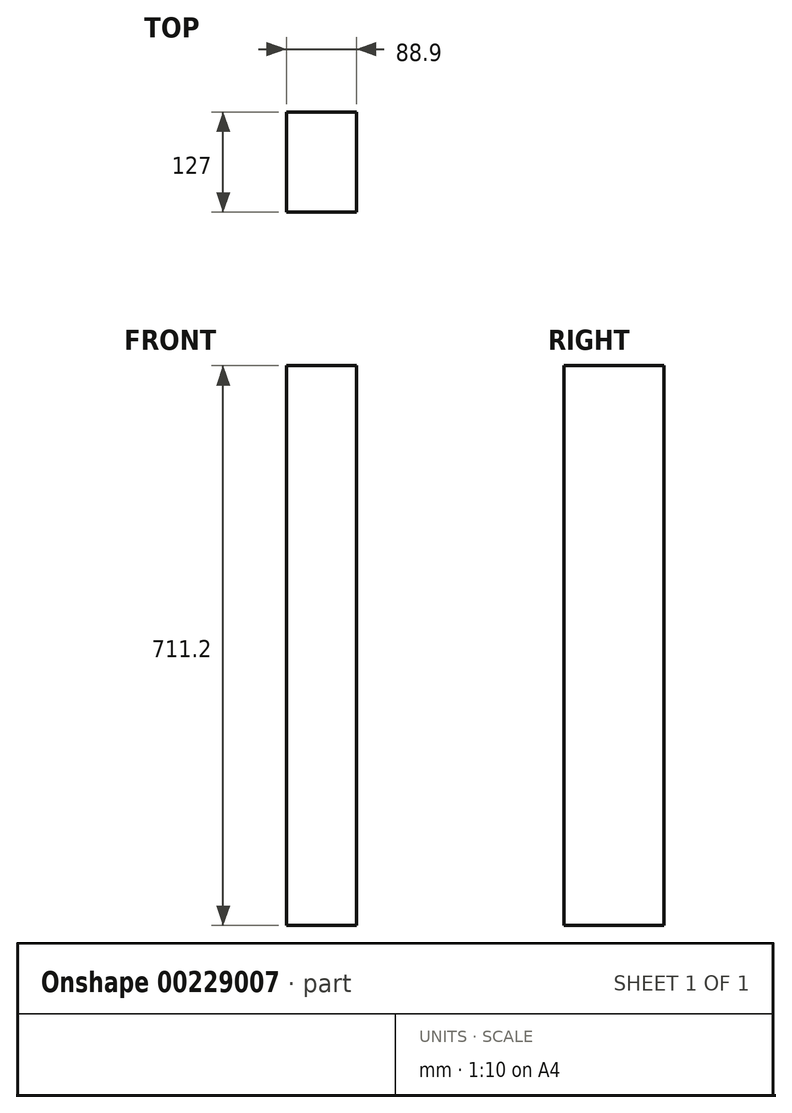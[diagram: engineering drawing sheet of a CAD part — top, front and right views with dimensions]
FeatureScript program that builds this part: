
annotation { "Feature Type Name" : "Feature", "Feature Type Description" : "" }
export const myFeature = defineFeature(function(context is Context, id is Id, definition is map)
    precondition{}
    {
        {
            var Q0;
            Q0=qCreatedBy(makeId("Top.planeOp"),FACE);
            var sketch = newSketch(context, id + "F0", { "sketchPlane" : qUnion([Q0])});
            skLineSegment(sketch, "E0.bottom", {"start": v(-42.17, 67) * mm, "end": v(46.73, 67) * mm});
            skLineSegment(sketch, "E0.top", {"start": v(-42.17, -60) * mm, "end": v(46.73, -60) * mm});
            skLineSegment(sketch, "E0.left", {"start": v(-42.17, 67) * mm, "end": v(-42.17, -60) * mm});
            skLineSegment(sketch, "E0.right", {"start": v(46.73, 67) * mm, "end": v(46.73, -60) * mm});
            skSolve(sketch);
        }
        {
            var Q0;
            Q0 = qSketchRegion(id + "F0", true);
            extrude(context, id + "F1", {"entities" : qUnion([Q0]), "depth" : 711.2 * mm});
        }
    });
